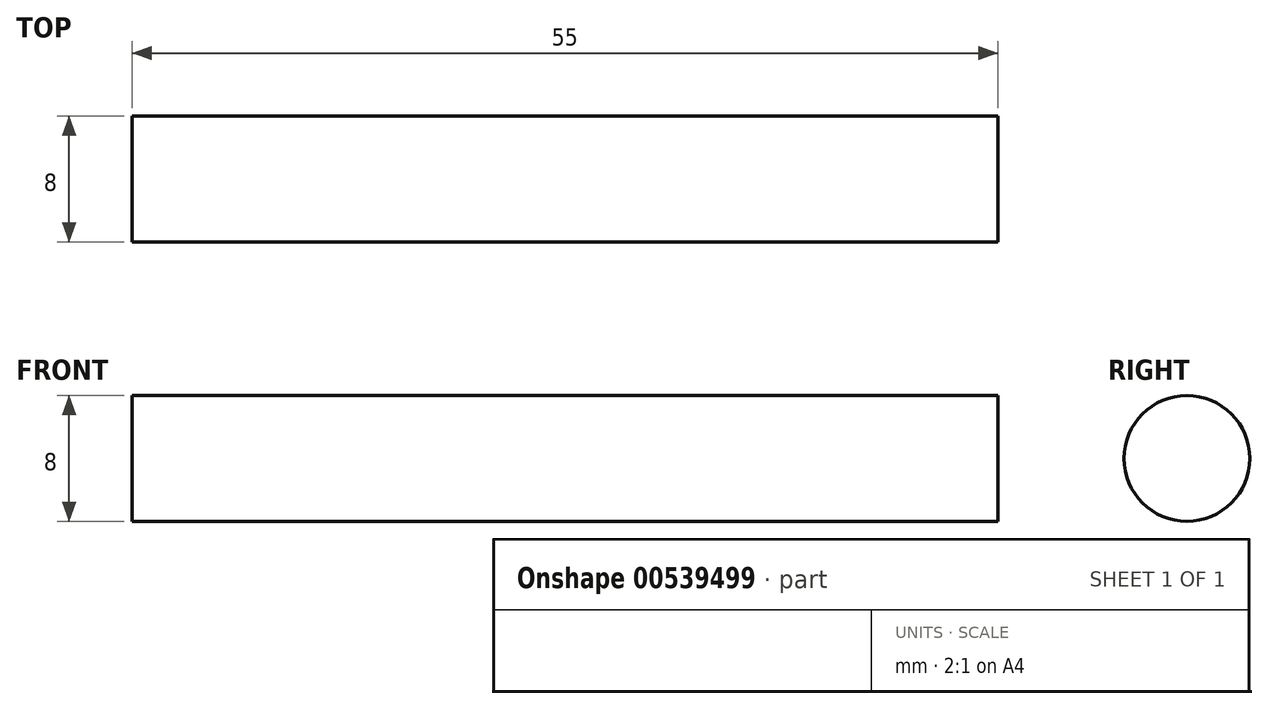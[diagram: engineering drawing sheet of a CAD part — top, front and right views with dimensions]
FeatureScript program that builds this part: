
annotation { "Feature Type Name" : "Feature", "Feature Type Description" : "" }
export const myFeature = defineFeature(function(context is Context, id is Id, definition is map)
    precondition{}
    {
        {
            var Q0;
            Q0=qCreatedBy(makeId("Right.planeOp"),FACE);
            var sketch = newSketch(context, id + "F0", { "sketchPlane" : qUnion([Q0])});
            skCircle(sketch, "E0", {"center": v(0, 0) * mm, "radius": 4 * mm});
            skSolve(sketch);
        }
        {
            var Q0;
            Q0 = qSketchRegion(id + "F0", true);
            extrude(context, id + "F1", {"entities" : qUnion([Q0]), "depth" : 55 * mm, "offsetDistance" : 25 * mm});
        }
    });
